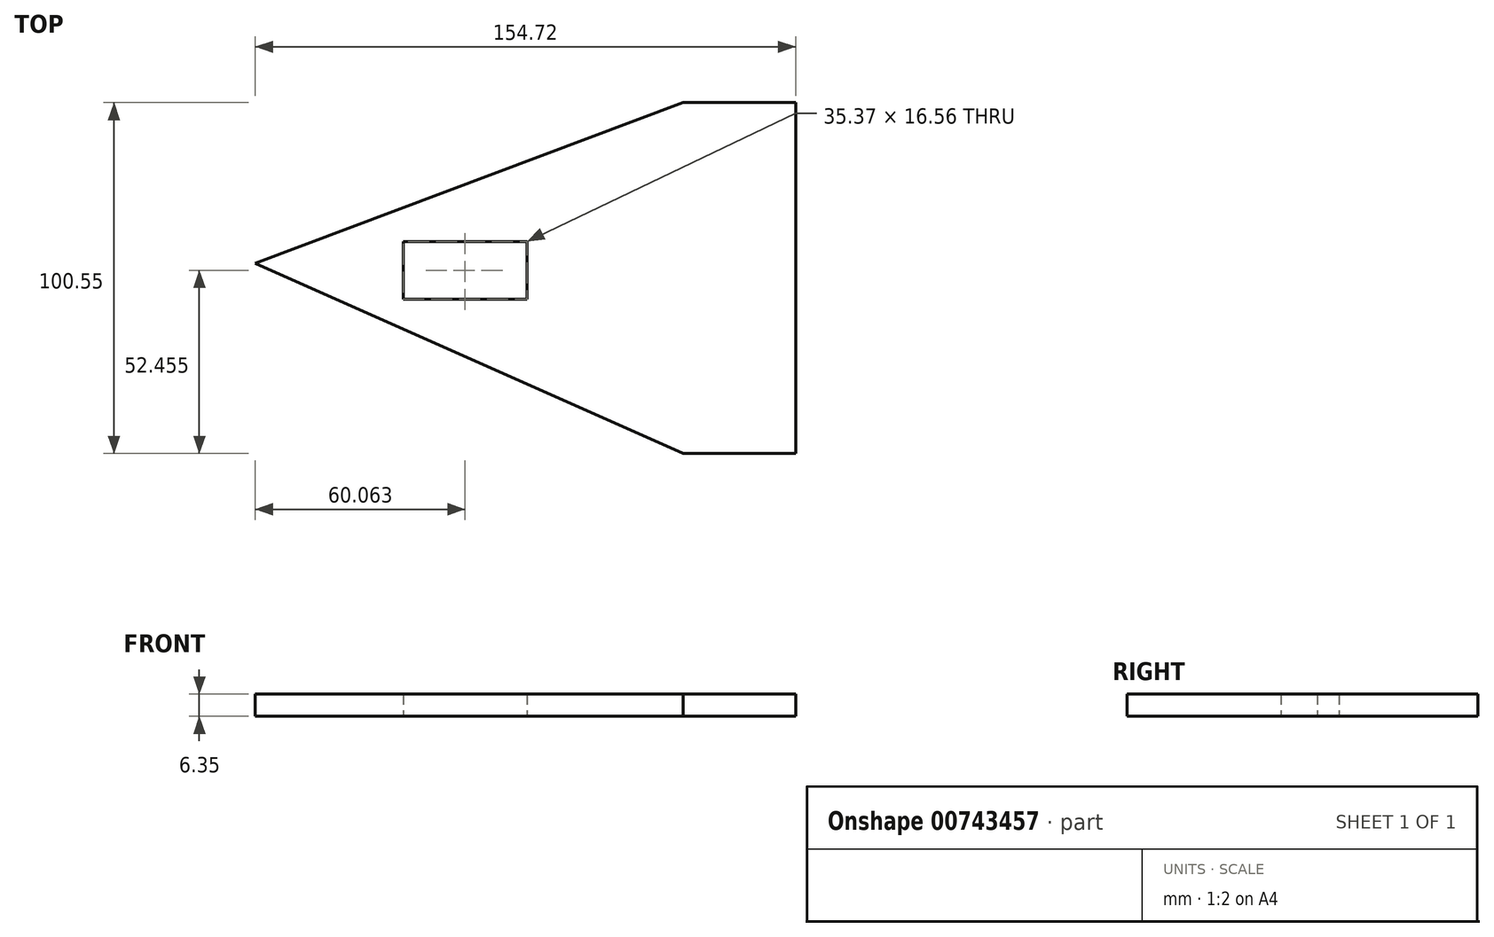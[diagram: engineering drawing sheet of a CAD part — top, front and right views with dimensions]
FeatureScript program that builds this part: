
annotation { "Feature Type Name" : "Feature", "Feature Type Description" : "" }
export const myFeature = defineFeature(function(context is Context, id is Id, definition is map)
    precondition{}
    {
        {
            var Q0;
            Q0=qCreatedBy(makeId("Top.planeOp"),FACE);
            var sketch = newSketch(context, id + "F0", { "sketchPlane" : qUnion([Q0])});
            skLineSegment(sketch, "E0.bottom", {"start": v(-42.38, 58.1) * mm, "end": v(112.34, 58.1) * mm});
            skLineSegment(sketch, "E0.top", {"start": v(-42.38, -68.9) * mm, "end": v(112.34, -68.9) * mm});
            skLineSegment(sketch, "E0.left", {"start": v(-42.38, 58.1) * mm, "end": v(-42.38, -68.9) * mm});
            skLineSegment(sketch, "E0.right", {"start": v(112.34, 58.1) * mm, "end": v(112.34, -68.9) * mm});
            skLineSegment(sketch, "E1", {"start": v(112.34, 58.1) * mm, "end": v(-42.38, 0) * mm});
            skLineSegment(sketch, "E2", {"start": v(-42.38, 0) * mm, "end": v(112.34, -68.9) * mm});
            skLineSegment(sketch, "E3.bottom", {"start": v(0, -10.38) * mm, "end": v(35.37, -10.38) * mm});
            skLineSegment(sketch, "E3.top", {"start": v(0, 6.19) * mm, "end": v(35.37, 6.19) * mm});
            skLineSegment(sketch, "E3.left", {"start": v(0, -10.38) * mm, "end": v(0, 6.19) * mm});
            skLineSegment(sketch, "E3.right", {"start": v(35.37, -10.38) * mm, "end": v(35.37, 6.19) * mm});
            skLineSegment(sketch, "E4", {"start": v(17.68, -10.38) * mm, "end": v(17.68, -26.75) * mm});
            skLineSegment(sketch, "E5", {"start": v(17.68, -10.38) * mm, "end": v(17.68, 6.19) * mm});
            skLineSegment(sketch, "E6", {"start": v(17.68, 22.56) * mm, "end": v(17.68, 6.19) * mm});
            skLineSegment(sketch, "E7", {"start": v(80.12, 46) * mm, "end": v(112.34, 46) * mm});
            skLineSegment(sketch, "E8", {"start": v(80.12, -54.55) * mm, "end": v(112.34, -54.55) * mm});
            skSolve(sketch);
        }
        {
            var Q0;
            {var subQ0=sQuery(id+"F0.wireOp",EDGE,"E3.right");Q0=makeQuery(id+"F0.imprint","IMPRINT",FACE,{"disambiguationData":[TD([[makeQuery(id+"F0.imprint","IMPRINT",EDGE,{"derivedFrom":subQ0}),-1.0]])]});}
            var Q1;
            {var subQ0=sQuery(id+"F0.wireOp",EDGE,"E3.left");Q1=makeQuery(id+"F0.imprint","IMPRINT",FACE,{"disambiguationData":[TD([[makeQuery(id+"F0.imprint","IMPRINT",EDGE,{"derivedFrom":subQ0}),1.0]])]});}
            extrude(context, id + "F1", {"entities" : qUnion([Q0, Q1]), "depth" : 6.35 * mm, "offsetDistance" : 25.4 * mm});
        }
    });
